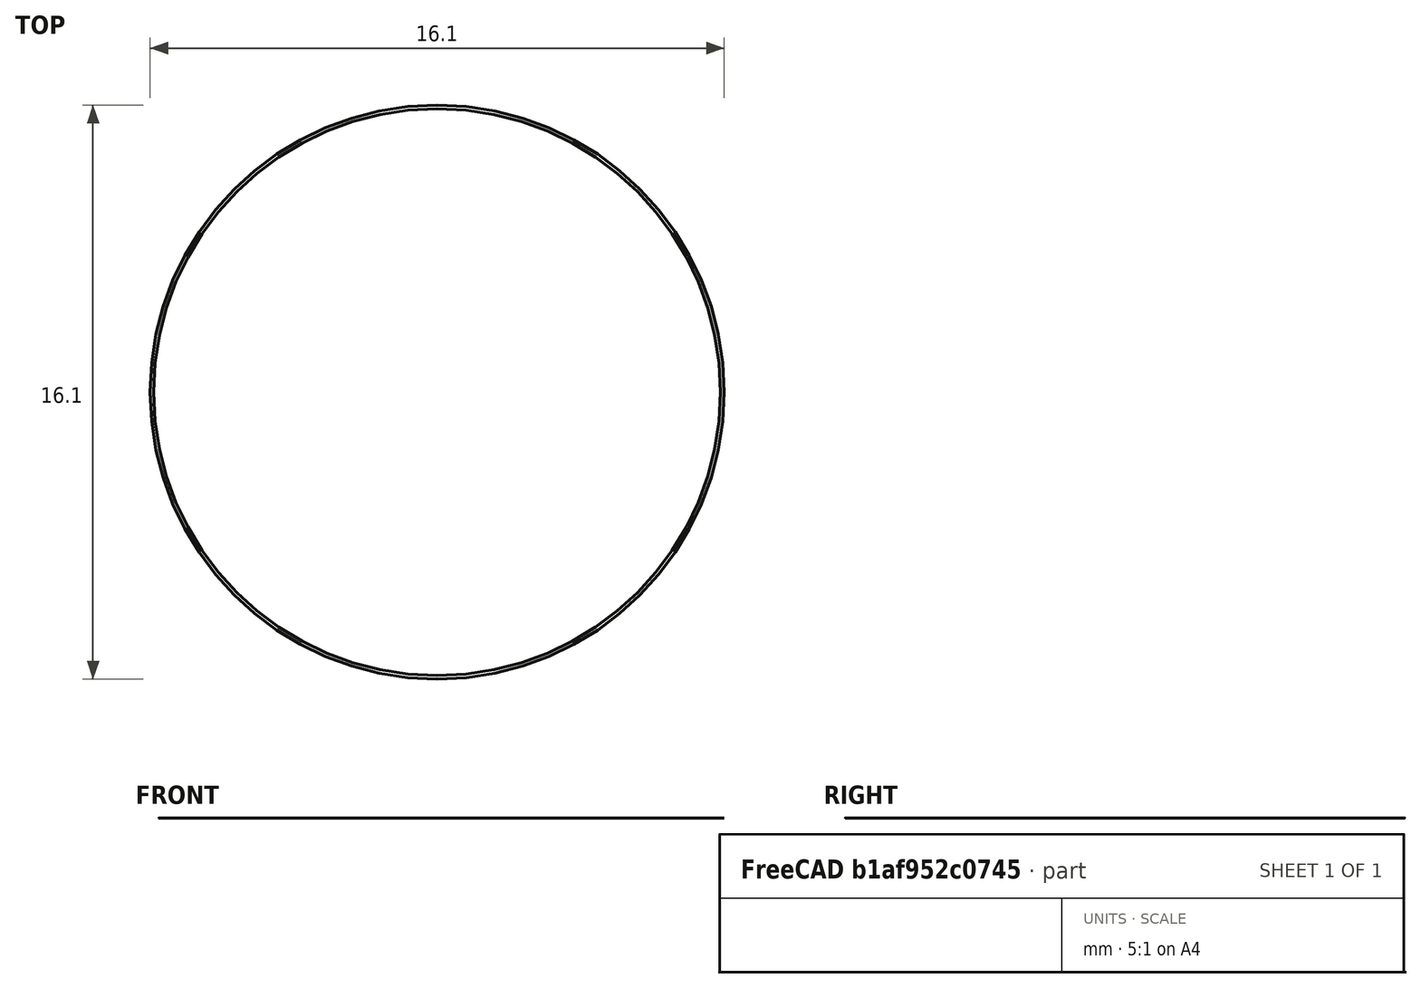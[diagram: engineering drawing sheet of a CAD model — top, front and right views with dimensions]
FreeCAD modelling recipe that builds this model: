
FCSTD DOCUMENT  (FreeCAD 0.21R33668 +26 (Git))
Label: conductor_and_outer_dielectric
License: All rights reserved
LicenseURL: http://en.wikipedia.org/wiki/All_rights_reserved
objects: Part::Part2DObjectPython×3, Spreadsheet::Sheet×1, Part::Cut×1
note: 4 computed .brp shape members not serialized (recipe doc carries the construction recipe); baked Part::Feature solids carry a one-line shape summary decoded from their .brp

FEATURE [Part::Part2DObjectPython] Circle006  label="Overbraid_internal"  # Draft 2D object (typed FeaturePython)
  Area = 203.583
  FirstAngle = 0
  LastAngle = 0
  MakeFace = true
  Radius = 8.05
  expr: Radius = <<Spreadsheet>>.OJ_outer_radius
FEATURE [Spreadsheet::Sheet] Spreadsheet
  cells = C1='Radius; D1='Insulation O.R.; B2='Overbraid Jacket (OJ); C2(OJ_radius)==7.95 mm; D2(OJ_outer_radius)==8.05 mm; B3='Shield (S); C3(S_radius)==4.5 / 2; B4='AWG 11; C4(AWG11)==2.3 mm / 2; D4(awg11_insulation_radius)==C4 + 0.1 mm; B5='AWG 17; C5(AWG17)==1.15 mm / 2; D5(awg17_insulation_radius)==C5 + 0.15 mm; B6='AWG 21; C6(AWG21)==0.72 mm / 2; D6(awg21_insulation_radius)==C6 + 0.1 mm; A8='Num; B8='AWG 11; C8='x; D8='y; A9=0; B9='A; C9(AWG_11_A_x)==-1.209 mm; D9(AWG_11_A_y)==5.934 mm; A10=1; B10='B; C10(AWG_11_B_x)==-3.734 mm; D10(AWG_11_B_y)=4.83; A11=2; B11='C; C11(AWG_11_C_x)==-5.595; D11(AWG_11_C_y)=2.349; A12=3; B12='D; C12(AWG_11_D_x)==-5.905; D12(AWG_11_D_y)==-0.548; A13=4; B13='E; C13(AWG_11_E_x)==-5.141; D13(AWG_11_E_y)==-3.16; A14=5; B14='F; C14(AWG_11_F_x)==-2.923; D14(AWG_11_F_y)==-5.378; A15=6; B15='G; C15(AWG_11_G_x)=6.545; D15(AWG_11_G_y)==-0.417; A16=7; B16='H; C16(AWG_11_H_x)=5.699; D16(AWG_11_H_y)=2.671; A17=8; B17='I; C17(AWG_11_I_x)=3.767; D17(AWG_11_I_y)=4.46; A18=9; B18='J; C18(AWG_11_J_x)=1.763; D18(AWG_11_J_y)=2.457; A19=10; B19='K; C19(AWG_11_K_x)=0.022; D19(AWG_11_K_y)=0.358; A20=11; B20='L; C20(AWG_11_L_x)==-1.015; D20(AWG_11_L_y)==-2.337; A21=12; B21='M; C21(AWG_11_M_x)=-2.983; D21(AWG_11_M_y)==-0.036; A22=13; B22='N; C22(AWG_11_N_x)=-1.683; D22(AWG_11_N_y)=2.314; A24='Num; B24='AWG 21; C24='x; D24='y; A25=14; B25='A; C25(AWG_21_A_x)==-0.097 mm; D25(AWG_21_A_y)==3.721 mm; A26=15; B26='B; C26(AWG_21_B_x)==-3.221; D26(AWG_21_B_y)==-2.325 mm; A27=16; B27='C; C27(AWG_21_C_x)=1.334; D27(AWG_21_C_y)==-1.359; A28=17; B28='D; C28(AWG_21_D_x)=3.588; D28(AWG_21_D_y)=1.443; A29=18; B29='E; C29(AWG_21_E_x)=4.578; D29(AWG_21_E_y)=0.203; A30=19; B30='F; C30(AWG_21_F_x)=4.399; D30(AWG_21_F_y)==-0.751; A31=20; B31='G; C31(AWG_21_G_x)=2.658; D31(AWG_21_G_y)==-1.24; A32=21; B32='H; C32(AWG_21_H_x)=3.779; D32(AWG_21_H_y)==-1.86; A33=22; B33='I; C33(AWG_21_I_x)=4.876; D33(AWG_21_I_y)==-2.552; A34=23; B34='J; C34(AWG_21_J_x)=6.235; D34(AWG_21_J_y)==-2.623; A35=24; B35='K; C35(AWG_21_K_x)=5.961; D35(AWG_21_K_y)==-3.661; A37='Num; B37='AWG 17; C37='x; D37='y; A38=25; B38='A; C38(AWG_17_A_x)==0.929 mm; D38(AWG_17_A_y)==6.547 mm; A39=26; B39='B; C39(AWG_17_B_x)==2.562 mm; D39(AWG_17_B_y)==6.213 mm; A40=27; B40='C; C40(AWG_17_C_x)=1.012; D40(AWG_17_C_y)==4.866 mm; A41=28; B41='D; C41(AWG_17_D_x)=2.562; D41(AWG_17_D_y)==0.251 mm; A42=29; B42='E; C42(AWG_17_E_x)==-1.087; D42(AWG_17_E_y)==-6.535 mm; A43=30; B43='S; C43(Shield_x)==2.336 mm; D43(Shield_y)==-4.901 mm; A45='Num; B45='AWG 17 within shield; C45='x; D45='y; A46=31; B46='F; C46=2.276; D46==-3.458; A47=32; B47='G; C47=0.893; D47==-4.412; A48=33; B48='H; C48=1.155; D48==-5.712; A49=34; B49='I; C49=2.431; D49==-6.332; A50=35; B50='J; C50=3.659; D50==-5.533; A51=36; B51='K; C51=3.648; D51==-4.198; A52=37; B52='L; C52=2.336; D52==-4.901
FEATURE [Part::Part2DObjectPython] Circle017  label="Conductor_000"  # Draft 2D object (typed FeaturePython)
  Area = 4.15476
  FirstAngle = 0
  LastAngle = 0
  MakeFace = true
  Placement = pos=(-1.209,5.934,0) rot=(-1.209,5.934,1;0rad)
  Radius = 1.15
  expr: .Placement.Base.x = <<Spreadsheet>>.AWG_11_A_x
  expr: .Placement.Base.y = <<Spreadsheet>>.AWG_11_A_y
  expr: .Placement.Rotation.Axis.x = <<Spreadsheet>>.AWG_11_A_x
  expr: .Placement.Rotation.Axis.y = <<Spreadsheet>>.AWG_11_A_y
  expr: Radius = <<Spreadsheet>>.AWG11
FEATURE [Part::Part2DObjectPython] Circle062  label="Overbraid_external"  # Draft 2D object (typed FeaturePython)
  Area = 198.557
  FirstAngle = 0
  LastAngle = 0
  MakeFace = true
  Radius = 7.95
  expr: Radius = <<Spreadsheet>>.OJ_radius
FEATURE [Part::Cut] Cut  label="Dielectric_000"
  Base = -> Circle006
  Tool = -> Circle062
